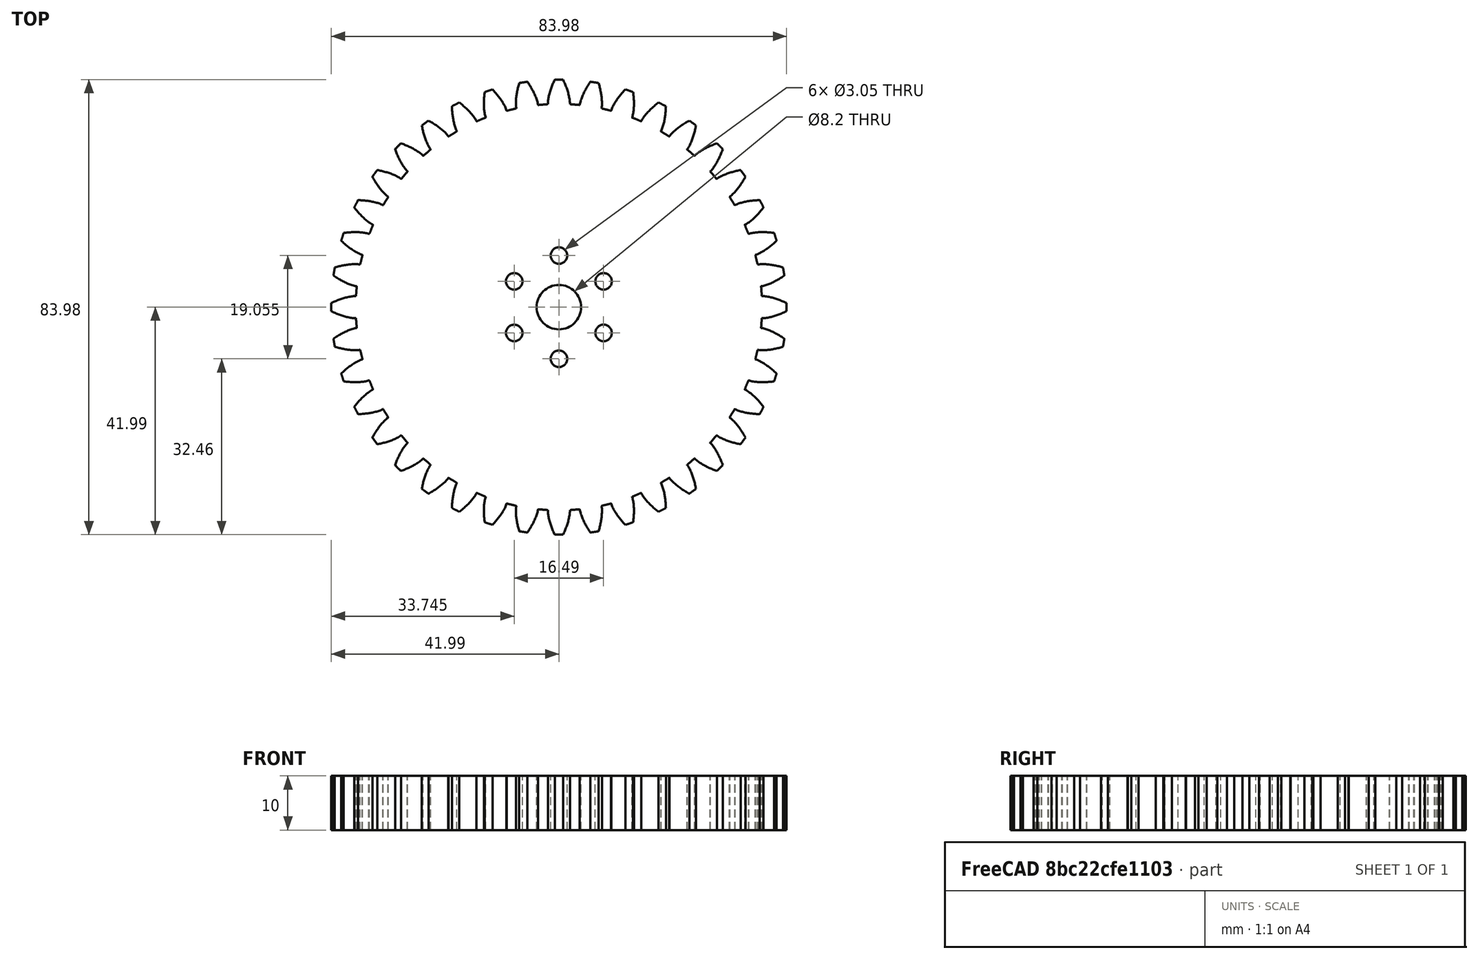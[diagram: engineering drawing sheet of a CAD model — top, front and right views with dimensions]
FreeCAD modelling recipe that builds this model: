
FCSTD DOCUMENT  (FreeCAD 0.19R17798 (Git))
Label: gear40
License: All rights reserved
LicenseURL: http://en.wikipedia.org/wiki/All_rights_reserved
objects: Part::Cylinder×7, Part::Cut×7, Part::FeaturePython×1
note: 15 computed .brp shape members not serialized (recipe doc carries the construction recipe); baked Part::Feature solids carry a one-line shape summary decoded from their .brp

FEATURE [Part::FeaturePython] InvoluteGear  # WARN: FeaturePython — macro-defined, semantics opaque (R4)
  backlash = 0
  beta = 0
  clearance = 0.25
  double_helix = false
  head = 0
  height = 10
  module = 2
  numpoints = 6
  pressure_angle = 20
  reversed_backlash = false
  shift = 0
  simple = false
  teeth = 40
  undercut = false
FEATURE [Part::Cylinder] Cylinder
  Angle = 360
  AttacherType = Attacher::AttachEngine3D
  Height = 30
  Placement = pos=(0,0,-10) rot=(0,0,1;0rad)
  Radius = 4.1
FEATURE [Part::Cylinder] Cylinder001
  Angle = 360
  AttacherType = Attacher::AttachEngine3D
  Height = 30
  Placement = pos=(8.245,4.762,-10) rot=(0,0,1;0rad)
  Radius = 1.525
FEATURE [Part::Cylinder] Cylinder002
  Angle = 360
  AttacherType = Attacher::AttachEngine3D
  Height = 30
  Placement = pos=(0,9.525,-10) rot=(0,0,1;0rad)
  Radius = 1.525
FEATURE [Part::Cylinder] Cylinder003
  Angle = 360
  AttacherType = Attacher::AttachEngine3D
  Height = 30
  Placement = pos=(-8.245,4.762,-10) rot=(0,0,1;0rad)
  Radius = 1.525
FEATURE [Part::Cylinder] Cylinder004
  Angle = 360
  AttacherType = Attacher::AttachEngine3D
  Height = 30
  Placement = pos=(-8.245,-4.762,-10) rot=(0,0,1;0rad)
  Radius = 1.525
FEATURE [Part::Cylinder] Cylinder005
  Angle = 360
  AttacherType = Attacher::AttachEngine3D
  Height = 30
  Placement = pos=(0,-9.53,-10) rot=(0,0,1;0rad)
  Radius = 1.525
FEATURE [Part::Cylinder] Cylinder006
  Angle = 360
  AttacherType = Attacher::AttachEngine3D
  Height = 30
  Placement = pos=(8.245,-4.76,-10) rot=(0,0,1;0rad)
  Radius = 1.525
FEATURE [Part::Cut] Cut
  Base = -> InvoluteGear
  Refine = true
  Tool = -> Cylinder
FEATURE [Part::Cut] Cut001
  Base = -> Cut
  Refine = true
  Tool = -> Cylinder001
FEATURE [Part::Cut] Cut002
  Base = -> Cut001
  Refine = true
  Tool = -> Cylinder002
FEATURE [Part::Cut] Cut003
  Base = -> Cut002
  Refine = true
  Tool = -> Cylinder003
FEATURE [Part::Cut] Cut004
  Base = -> Cut003
  Refine = true
  Tool = -> Cylinder004
FEATURE [Part::Cut] Cut005
  Base = -> Cut004
  Refine = true
  Tool = -> Cylinder005
FEATURE [Part::Cut] Cut006
  Base = -> Cut005
  Refine = true
  Tool = -> Cylinder006
